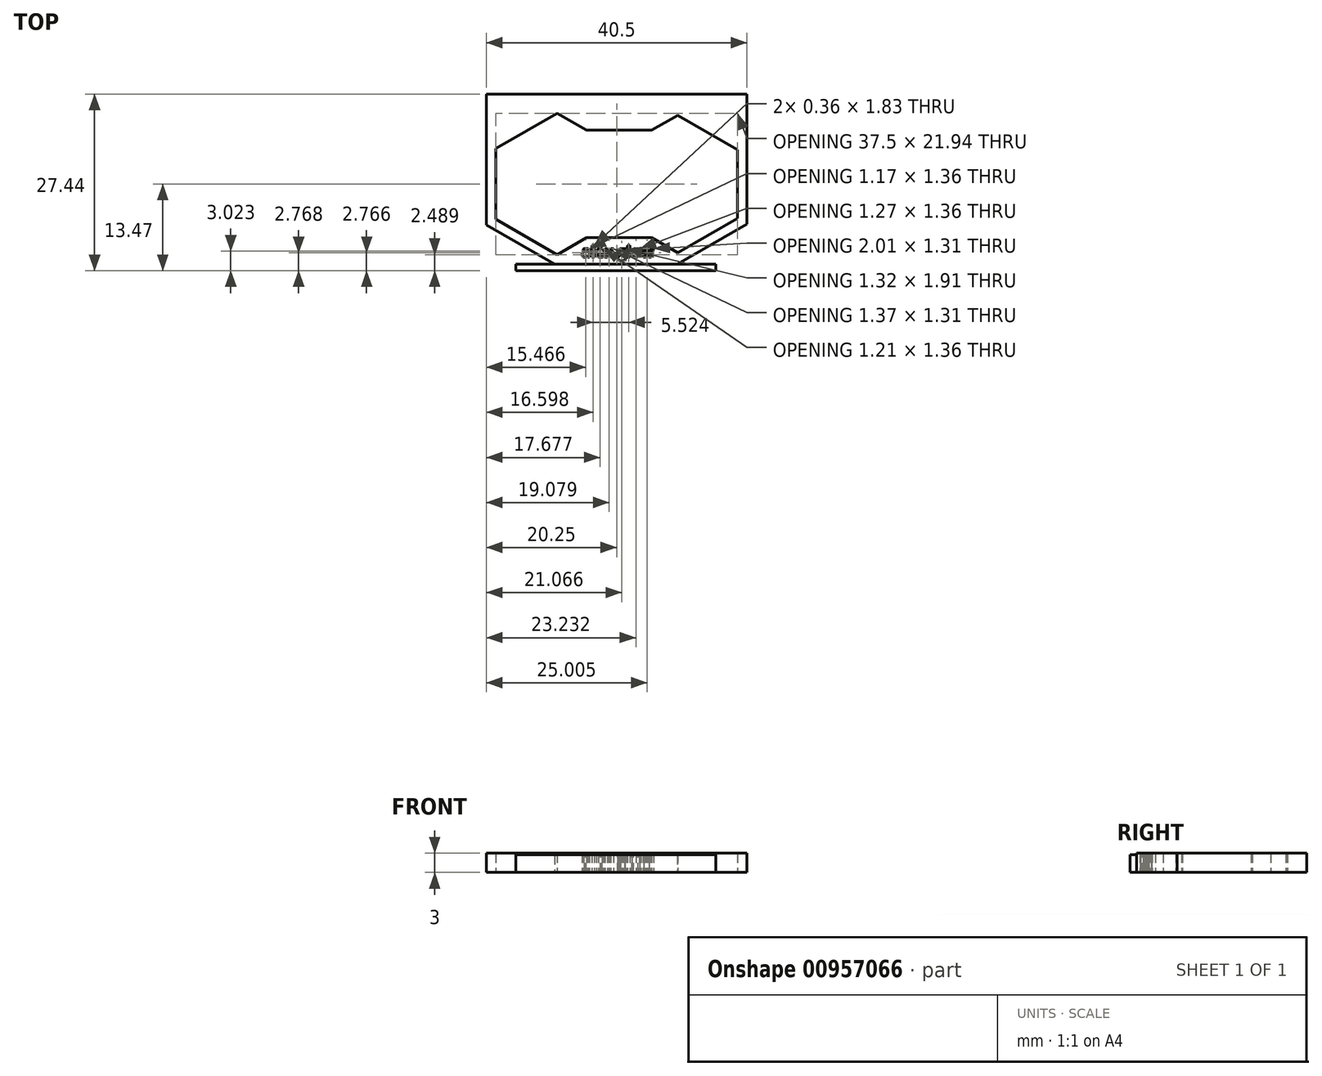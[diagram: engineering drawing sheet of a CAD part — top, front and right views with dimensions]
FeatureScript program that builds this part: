
annotation { "Feature Type Name" : "Feature", "Feature Type Description" : "" }
export const myFeature = defineFeature(function(context is Context, id is Id, definition is map)
    precondition{}
    {
        {
            var Q0;
            Q0=qCreatedBy(makeId("Top.planeOp"),FACE);
            var sketch = newSketch(context, id + "F0", { "sketchPlane" : qUnion([Q0])});
            skCircle(sketch, "E0.cCircle", {"center": v(-9.5, 0) * mm, "radius": 9.5 * mm, "construction": true});
            skLineSegment(sketch, "E0.0", {"start": v(0, 5.48) * mm, "end": v(0, -5.48) * mm});
            skLineSegment(sketch, "E0.1", {"start": v(0, -5.48) * mm, "end": v(-9.5, -10.97) * mm});
            skLineSegment(sketch, "E0.2", {"start": v(-9.5, -10.97) * mm, "end": v(-19, -5.48) * mm});
            skLineSegment(sketch, "E0.3", {"start": v(-19, -5.48) * mm, "end": v(-19, 5.48) * mm});
            skLineSegment(sketch, "E0.4", {"start": v(-19, 5.48) * mm, "end": v(-9.5, 10.97) * mm});
            skLineSegment(sketch, "E0.5", {"start": v(-9.5, 10.97) * mm, "end": v(0, 5.48) * mm});
            skPoint(sketch, "E0.0.midPoint", {"position": v(0, 0) * mm});
            skCircle(sketch, "E1.cCircle", {"center": v(9.25, 0) * mm, "radius": 9.25 * mm, "construction": true});
            skLineSegment(sketch, "E1.0", {"start": v(18.5, 5.34) * mm, "end": v(18.5, -5.34) * mm});
            skLineSegment(sketch, "E1.1", {"start": v(18.5, -5.34) * mm, "end": v(9.25, -10.68) * mm});
            skLineSegment(sketch, "E1.2", {"start": v(9.25, -10.68) * mm, "end": v(0, -5.34) * mm});
            skLineSegment(sketch, "E1.3", {"start": v(0, -5.34) * mm, "end": v(0, 5.34) * mm});
            skLineSegment(sketch, "E1.4", {"start": v(0, 5.34) * mm, "end": v(9.25, 10.68) * mm});
            skLineSegment(sketch, "E1.5", {"start": v(9.25, 10.68) * mm, "end": v(18.5, 5.34) * mm});
            skPoint(sketch, "E1.0.midPoint", {"position": v(18.5, 0) * mm});
            skLineSegment(sketch, "E2.bottom", {"start": v(-20.5, 13.97) * mm, "end": v(20, 13.97) * mm});
            skLineSegment(sketch, "E2.top", {"start": v(-20.5, -12.47) * mm, "end": v(20, -12.47) * mm});
            skLineSegment(sketch, "E2.left", {"start": v(-20.5, 13.97) * mm, "end": v(-20.5, -12.47) * mm});
            skLineSegment(sketch, "E2.right", {"start": v(20, 13.97) * mm, "end": v(20, -12.47) * mm});
            skLineSegment(sketch, "E3", {"start": v(-20.5, -6.35) * mm, "end": v(-9.9, -12.47) * mm});
            skLineSegment(sketch, "E4", {"start": v(20, -6.2) * mm, "end": v(9.15, -12.47) * mm});
            skPoint(sketch, "E5", {"position": v(0, 8.34) * mm});
            skPoint(sketch, "E6", {"position": v(0, -8.34) * mm});
            skLineSegment(sketch, "E7", {"start": v(-4.95, 8.34) * mm, "end": v(5.2, 8.34) * mm});
            skLineSegment(sketch, "E8", {"start": v(-4.95, -8.34) * mm, "end": v(5.2, -8.34) * mm});
            skText(sketch, "E9", { "text": "alex glow", "fontName": "OpenSans-Bold.ttf"});
            const initialGuessF0  = {"E9": [-0.00572, -0.01136, 1, 0, 0.00173]};
            skSetInitialGuess(sketch, initialGuessF0);
            skSolve(sketch);
        }
        {
            var Q0;
            {var subQ10=sQuery(id+"F0.wireOp",EDGE,"E0.2");Q0=makeQuery(id+"F0.imprint","IMPRINT",FACE,{"disambiguationData":[TD([[makeQuery(id+"F0.imprint","IMPRINT",EDGE,{"derivedFrom":subQ10}),1.0]])]});}
            extrude(context, id + "F1", {"entities" : qUnion([Q0]), "depth" : 3 * mm, "offsetDistance" : 25 * mm});
        }
        {
            var Q0;
            Q0=makeQuery(id+"F1.opExtrude","SWEPT_FACE",FACE,{"disambiguationData":[OSD([sQuery(id+"F0.wireOp",EDGE,"E2.top")])]});
            var sketch = newSketch(context, id + "F2", { "sketchPlane" : qUnion([Q0])});
            skLineSegment(sketch, "E10.bottom", {"start": v(-15.9, 3) * mm, "end": v(15.15, 3) * mm});
            skLineSegment(sketch, "E10.top", {"start": v(-15.9, 0) * mm, "end": v(15.15, 0) * mm});
            skLineSegment(sketch, "E10.left", {"start": v(-15.9, 3) * mm, "end": v(-15.9, 0) * mm});
            skLineSegment(sketch, "E10.right", {"start": v(15.15, 3) * mm, "end": v(15.15, 0) * mm});
            skLineSegment(sketch, "E11.bottom", {"start": v(-15.9, 2.75) * mm, "end": v(15.15, 2.75) * mm});
            skLineSegment(sketch, "E11.left", {"start": v(-15.9, 2.75) * mm, "end": v(-15.9, 0) * mm});
            skLineSegment(sketch, "E11.right", {"start": v(15.15, 2.75) * mm, "end": v(15.15, 0) * mm});
            skSolve(sketch);
        }
        {
            var Q0;
            {var subQ0=sQuery(id+"F2.wireOp",EDGE,"E10.top");var subQ3=sQuery(id+"F2.wireOp",EDGE,"E10.left");var subQ4=makeQuery(id+"F2.imprint","INTERSECT",VERTEX,{"derivedFrom":[subQ0,subQ3]});Q0=makeQuery(id+"F2.imprint","IMPRINT",FACE,{"disambiguationData":[TD([[makeQuery(id+"F2.imprint","IMPRINT",EDGE,{"disambiguationData":[TD([[subQ4,1.0]])],"derivedFrom":subQ3}),1.0]])]});}
            var Q1;
            {var subQ0=sQuery(id+"F2.wireOp",EDGE,"E10.top");var subQ1=sQuery(id+"F0.wireOp",EDGE,"E2.top");var subQ2=makeQuery(id+"F1.opExtrude","SWEPT_EDGE",EDGE,{"disambiguationData":[OSD([subQ1,sQuery(id+"F0.wireOp",EDGE,"E3")])]});var subQ3=makeQuery(id+"F2.imprint","INTERSECT",VERTEX,{"derivedFrom":[subQ2,subQ0]});Q1=makeQuery(id+"F2.imprint","IMPRINT",FACE,{"disambiguationData":[TD([[makeQuery(id+"F2.imprint","IMPRINT",EDGE,{"disambiguationData":[TD([[subQ3,-1.0]])],"derivedFrom":subQ0}),1.0]])]});}
            var Q2;
            {var subQ0=sQuery(id+"F2.wireOp",EDGE,"E10.top");var subQ3=sQuery(id+"F2.wireOp",EDGE,"E10.right");var subQ4=makeQuery(id+"F2.imprint","INTERSECT",VERTEX,{"derivedFrom":[subQ0,subQ3]});Q2=makeQuery(id+"F2.imprint","IMPRINT",FACE,{"disambiguationData":[TD([[makeQuery(id+"F2.imprint","IMPRINT",EDGE,{"disambiguationData":[TD([[subQ4,1.0]])],"derivedFrom":subQ3}),-1.0]])]});}
            extrude(context, id + "F3", {"entities" : qUnion([Q0, Q1, Q2]), "operationType" : NewBodyOperationType.ADD, "depth" : 1 * mm, "offsetDistance" : 25 * mm});
        }
    });
